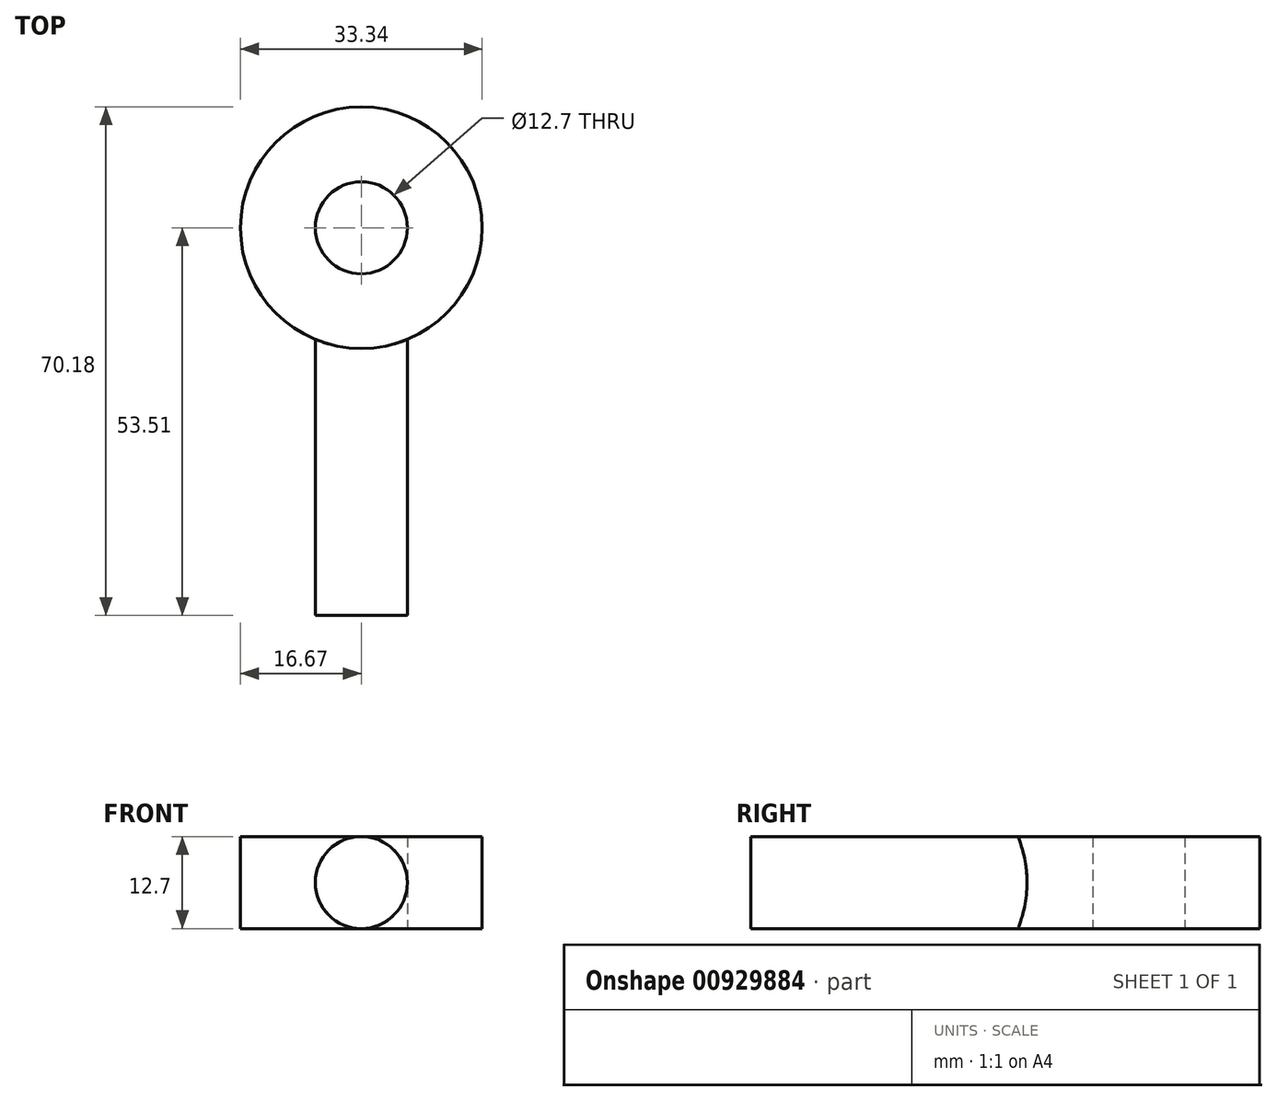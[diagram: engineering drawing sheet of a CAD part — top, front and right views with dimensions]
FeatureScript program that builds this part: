
annotation { "Feature Type Name" : "Feature", "Feature Type Description" : "" }
export const myFeature = defineFeature(function(context is Context, id is Id, definition is map)
    precondition{}
    {
        {
            var Q0;
            Q0=qCreatedBy(makeId("Top.planeOp"),FACE);
            var sketch = newSketch(context, id + "F0", { "sketchPlane" : qUnion([Q0])});
            skLineSegment(sketch, "E0", {"start": v(-6.35, -15.41) * mm, "end": v(-6.35, -53.51) * mm});
            skLineSegment(sketch, "E1", {"start": v(-6.35, -53.51) * mm, "end": v(6.35, -53.51) * mm});
            skLineSegment(sketch, "E2", {"start": v(6.35, -53.51) * mm, "end": v(6.35, -15.41) * mm});
            skCircle(sketch, "E3", {"center": v(0, 0) * mm, "radius": 6.35 * mm});
            skArc(sketch, "E4", {"start": v(6.35, -15.41) * mm, "mid": v(0, 16.67) * mm, "end": v(-6.35, -15.41) * mm});
            skSolve(sketch);
        }
        {
            var Q0;
            Q0=makeQuery(id+"F0.imprint","IMPRINT",FACE,{"disambiguationData":[TD([[makeQuery(id+"F0.imprint","IMPRINT",EDGE,{"derivedFrom":sQuery(id+"F0.wireOp",EDGE,"E0")}),1.0]])]});
            extrude(context, id + "F1", {"entities" : qUnion([Q0]), "endBound" : BoundingType.SYMMETRIC, "depth" : 12.7 * mm, "offsetDistance" : 25.4 * mm});
        }
        {
            var Q0;
            Q0=makeQuery(id+"F1.opExtrude","CAP_EDGE",EDGE,{"disambiguationData":[OSD([sQuery(id+"F0.wireOp",EDGE,"E0")])],"isStart":true});
            var Q1;
            Q1=makeQuery(id+"F1.opExtrude","CAP_EDGE",EDGE,{"disambiguationData":[OSD([sQuery(id+"F0.wireOp",EDGE,"E2")])],"isStart":true});
            var Q2;
            Q2=makeQuery(id+"F1.opExtrude","CAP_EDGE",EDGE,{"disambiguationData":[OSD([sQuery(id+"F0.wireOp",EDGE,"E0")])],"isStart":false});
            var Q3;
            Q3=makeQuery(id+"F1.opExtrude","CAP_EDGE",EDGE,{"disambiguationData":[OSD([sQuery(id+"F0.wireOp",EDGE,"E2")])],"isStart":false});
            fillet(context, id + "F2", {"entities" : qUnion([Q0, Q1, Q2, Q3]), "radius" : 6.35 * mm, "tangentPropagation" : true, "allowEdgeOverflow" : false});
        }
    });
